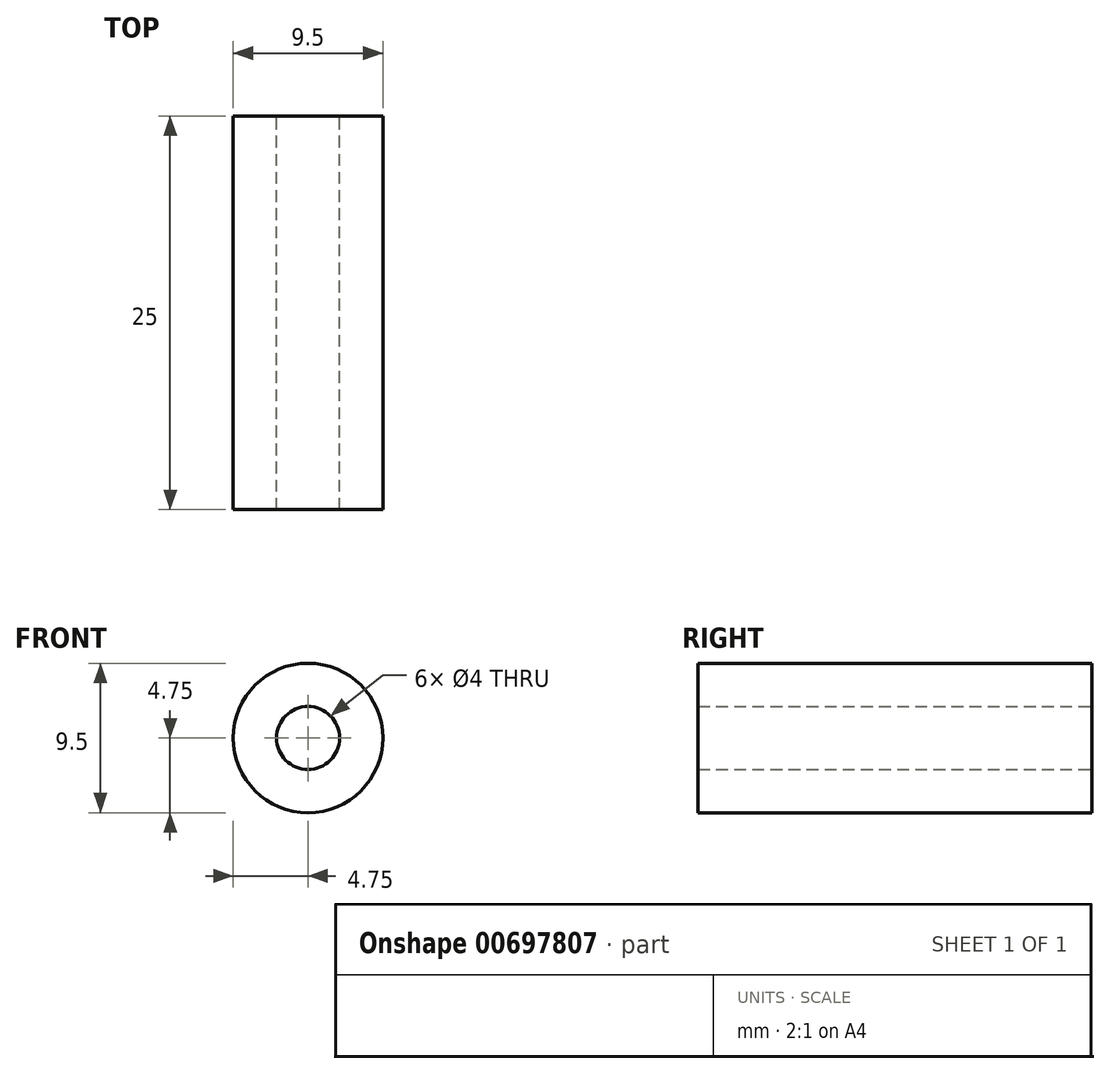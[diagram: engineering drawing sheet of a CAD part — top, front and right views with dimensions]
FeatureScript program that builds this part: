
annotation { "Feature Type Name" : "Feature", "Feature Type Description" : "" }
export const myFeature = defineFeature(function(context is Context, id is Id, definition is map)
    precondition{}
    {
        {
            var Q0;
            Q0=qCreatedBy(makeId("Front.planeOp"),FACE);
            var sketch = newSketch(context, id + "F0", { "sketchPlane" : qUnion([Q0])});
            skCircle(sketch, "E0", {"center": v(0, 0) * mm, "radius": 4.75 * mm});
            skCircle(sketch, "E1", {"center": v(0, 0) * mm, "radius": 2 * mm});
            skSolve(sketch);
        }
        {
            var Q0;
            Q0=qSketchRegion(id+"F0",true);
            extrude(context, id + "F1", {"entities" : qUnion([Q0]), "depth" : 25 * mm, "offsetDistance" : 25 * mm});
        }
    });
